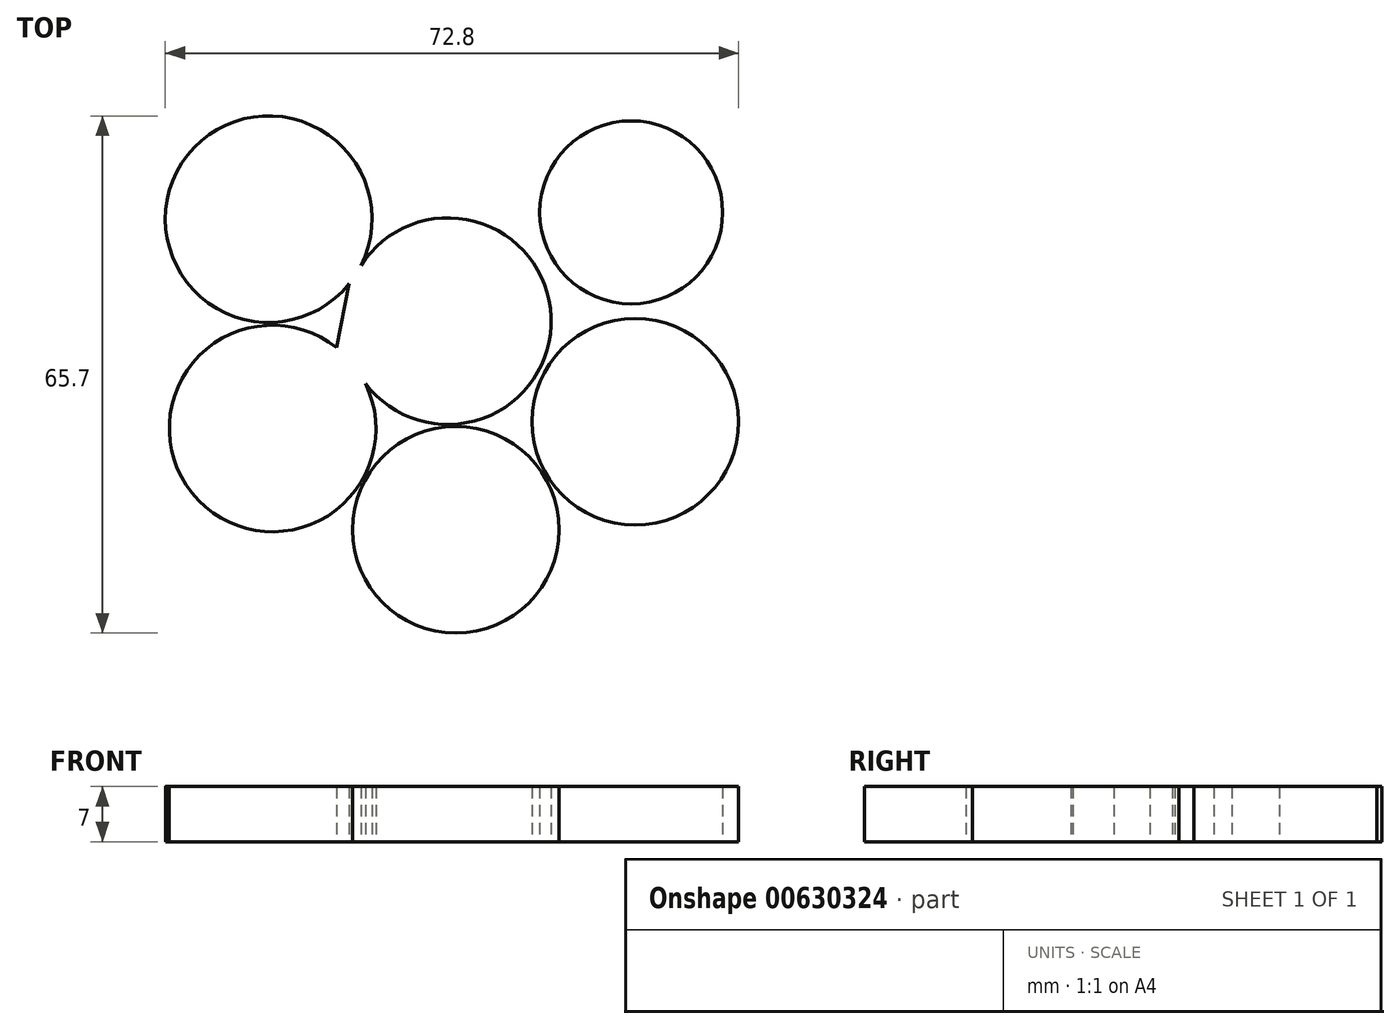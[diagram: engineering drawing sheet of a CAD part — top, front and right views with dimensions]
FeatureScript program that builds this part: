
annotation { "Feature Type Name" : "Feature", "Feature Type Description" : "" }
export const myFeature = defineFeature(function(context is Context, id is Id, definition is map)
    precondition{}
    {
        {
            var Q0;
            Q0=qCreatedBy(makeId("Top.planeOp"),FACE);
            var sketch = newSketch(context, id + "F0", { "sketchPlane" : qUnion([Q0])});
            skCircle(sketch, "E0", {"center": v(0, 0) * mm, "radius": 11.62 * mm});
            skCircle(sketch, "E1", {"center": v(0, 26.69) * mm, "radius": 11.62 * mm});
            skCircle(sketch, "E2", {"center": v(0, 26.69) * mm, "radius": 13.12 * mm});
            skCircle(sketch, "E3", {"center": v(0, 0) * mm, "radius": 13.12 * mm});
            skCircle(sketch, "E4.1.0", {"center": v(-22.78, 12.96) * mm, "radius": 13.12 * mm});
            skCircle(sketch, "E4.1.1", {"center": v(-22.78, 12.96) * mm, "radius": 11.62 * mm});
            skCircle(sketch, "E4.2.0", {"center": v(-22.28, -13.63) * mm, "radius": 13.12 * mm});
            skCircle(sketch, "E4.2.1", {"center": v(-22.28, -13.63) * mm, "radius": 11.62 * mm});
            skPoint(sketch, "E4.center", {"position": v(0.5, 0.1) * mm});
            skCircle(sketch, "E5.1.3.0", {"center": v(1, -26.5) * mm, "radius": 13.12 * mm});
            skCircle(sketch, "E5.2.3.0", {"center": v(1, -26.5) * mm, "radius": 11.62 * mm});
            skCircle(sketch, "E5.1.4.0", {"center": v(23.78, -12.77) * mm, "radius": 13.12 * mm});
            skCircle(sketch, "E5.2.4.0", {"center": v(23.78, -12.77) * mm, "radius": 11.62 * mm});
            skCircle(sketch, "E5.1.5.0", {"center": v(23.28, 13.83) * mm, "radius": 13.12 * mm});
            skCircle(sketch, "E5.2.5.0", {"center": v(23.28, 13.83) * mm, "radius": 11.62 * mm});
            skLineSegment(sketch, "E6", {"start": v(12.28, -11.1) * mm, "end": v(6.95, -9.31) * mm});
            skLineSegment(sketch, "E7", {"start": v(-5.48, -15.09) * mm, "end": v(-10.45, -7.95) * mm});
            skLineSegment(sketch, "E8", {"start": v(-14.13, -3.35) * mm, "end": v(-12.54, 4.75) * mm});
            skLineSegment(sketch, "E9", {"start": v(-9.66, 12.96) * mm, "end": v(-3.3, 15.55) * mm});
            skLineSegment(sketch, "E10", {"start": v(6.17, 15.1) * mm, "end": v(10.29, 12) * mm});
            skSolve(sketch);
        }
        {
            var Q0;
            Q0=makeQuery(id+"F0.imprint","IMPRINT",FACE,{"disambiguationData":[TD([[makeQuery(id+"F0.imprint","IMPRINT",EDGE,{"derivedFrom":sQuery(id+"F0.wireOp",EDGE,"E4.2.1")}),1.0]])]});
            var Q1;
            Q1=makeQuery(id+"F0.imprint","IMPRINT",FACE,{"disambiguationData":[TD([[makeQuery(id+"F0.imprint","IMPRINT",EDGE,{"derivedFrom":sQuery(id+"F0.wireOp",EDGE,"E5.1.3.0")}),1.0]])]});
            var Q2;
            Q2=makeQuery(id+"F0.imprint","IMPRINT",FACE,{"disambiguationData":[TD([[makeQuery(id+"F0.imprint","IMPRINT",EDGE,{"derivedFrom":sQuery(id+"F0.wireOp",EDGE,"E0")}),1.0]])]});
            var Q3;
            Q3=makeQuery(id+"F0.imprint","IMPRINT",FACE,{"disambiguationData":[TD([[makeQuery(id+"F0.imprint","IMPRINT",EDGE,{"derivedFrom":sQuery(id+"F0.wireOp",EDGE,"E0")}),-1.0]])]});
            var Q4;
            Q4=makeQuery(id+"F0.imprint","IMPRINT",FACE,{"disambiguationData":[TD([[makeQuery(id+"F0.imprint","IMPRINT",EDGE,{"derivedFrom":sQuery(id+"F0.wireOp",EDGE,"E4.1.1")}),-1.0]])]});
            var Q5;
            Q5=makeQuery(id+"F0.imprint","IMPRINT",FACE,{"disambiguationData":[TD([[makeQuery(id+"F0.imprint","IMPRINT",EDGE,{"derivedFrom":sQuery(id+"F0.wireOp",EDGE,"E4.2.1")}),-1.0]])]});
            var Q6;
            Q6=makeQuery(id+"F0.imprint","IMPRINT",FACE,{"disambiguationData":[TD([[makeQuery(id+"F0.imprint","IMPRINT",EDGE,{"derivedFrom":sQuery(id+"F0.wireOp",EDGE,"E4.1.1")}),1.0]])]});
            var Q7;
            Q7=makeQuery(id+"F0.imprint","IMPRINT",FACE,{"disambiguationData":[TD([[makeQuery(id+"F0.imprint","IMPRINT",EDGE,{"derivedFrom":sQuery(id+"F0.wireOp",EDGE,"E5.2.3.0")}),1.0]])]});
            var Q8;
            Q8=makeQuery(id+"F0.imprint","IMPRINT",FACE,{"disambiguationData":[TD([[makeQuery(id+"F0.imprint","IMPRINT",EDGE,{"derivedFrom":sQuery(id+"F0.wireOp",EDGE,"E5.2.4.0")}),1.0]])]});
            var Q9;
            Q9=makeQuery(id+"F0.imprint","IMPRINT",FACE,{"disambiguationData":[TD([[makeQuery(id+"F0.imprint","IMPRINT",EDGE,{"derivedFrom":sQuery(id+"F0.wireOp",EDGE,"E5.1.4.0")}),1.0]])]});
            var Q10;
            Q10=makeQuery(id+"F0.imprint","IMPRINT",FACE,{"disambiguationData":[TD([[makeQuery(id+"F0.imprint","IMPRINT",EDGE,{"derivedFrom":sQuery(id+"F0.wireOp",EDGE,"E5.2.5.0")}),1.0]])]});
            var Q11;
            {var subQ5=sQuery(id+"F0.wireOp",EDGE,"E8");Q11=makeQuery(id+"F0.imprint","IMPRINT",FACE,{"disambiguationData":[TD([[makeQuery(id+"F0.imprint","IMPRINT",EDGE,{"derivedFrom":subQ5}),-1.0]])]});}
            var Q12;
            {var subQ0=sQuery(id+"F0.wireOp",EDGE,"E4.1.0");var subQ1=sQuery(id+"F0.wireOp",EDGE,"E3");var subQ2=makeQuery(id+"F0.imprint","INTERSECT",VERTEX,{"disambiguationData":[OD(0.0)],"derivedFrom":[subQ1,subQ0]});Q12=makeQuery(id+"F0.imprint","IMPRINT",FACE,{"disambiguationData":[TD([[makeQuery(id+"F0.imprint","IMPRINT",EDGE,{"disambiguationData":[TD([[subQ2,-1.0]])],"derivedFrom":subQ1}),1.0]])]});}
            var Q13;
            {var subQ0=sQuery(id+"F0.wireOp",EDGE,"E4.2.0");var subQ1=sQuery(id+"F0.wireOp",EDGE,"E3");var subQ2=makeQuery(id+"F0.imprint","INTERSECT",VERTEX,{"disambiguationData":[OD(0.0)],"derivedFrom":[subQ1,subQ0]});Q13=makeQuery(id+"F0.imprint","IMPRINT",FACE,{"disambiguationData":[TD([[makeQuery(id+"F0.imprint","IMPRINT",EDGE,{"disambiguationData":[TD([[subQ2,1.0]])],"derivedFrom":subQ1}),1.0]])]});}
            extrude(context, id + "F1", {"entities" : qUnion([Q0, Q1, Q2, Q3, Q4, Q5, Q6, Q7, Q8, Q9, Q10, Q11, Q12, Q13]), "depth" : 7 * mm, "offsetDistance" : 25 * mm});
        }
    });
